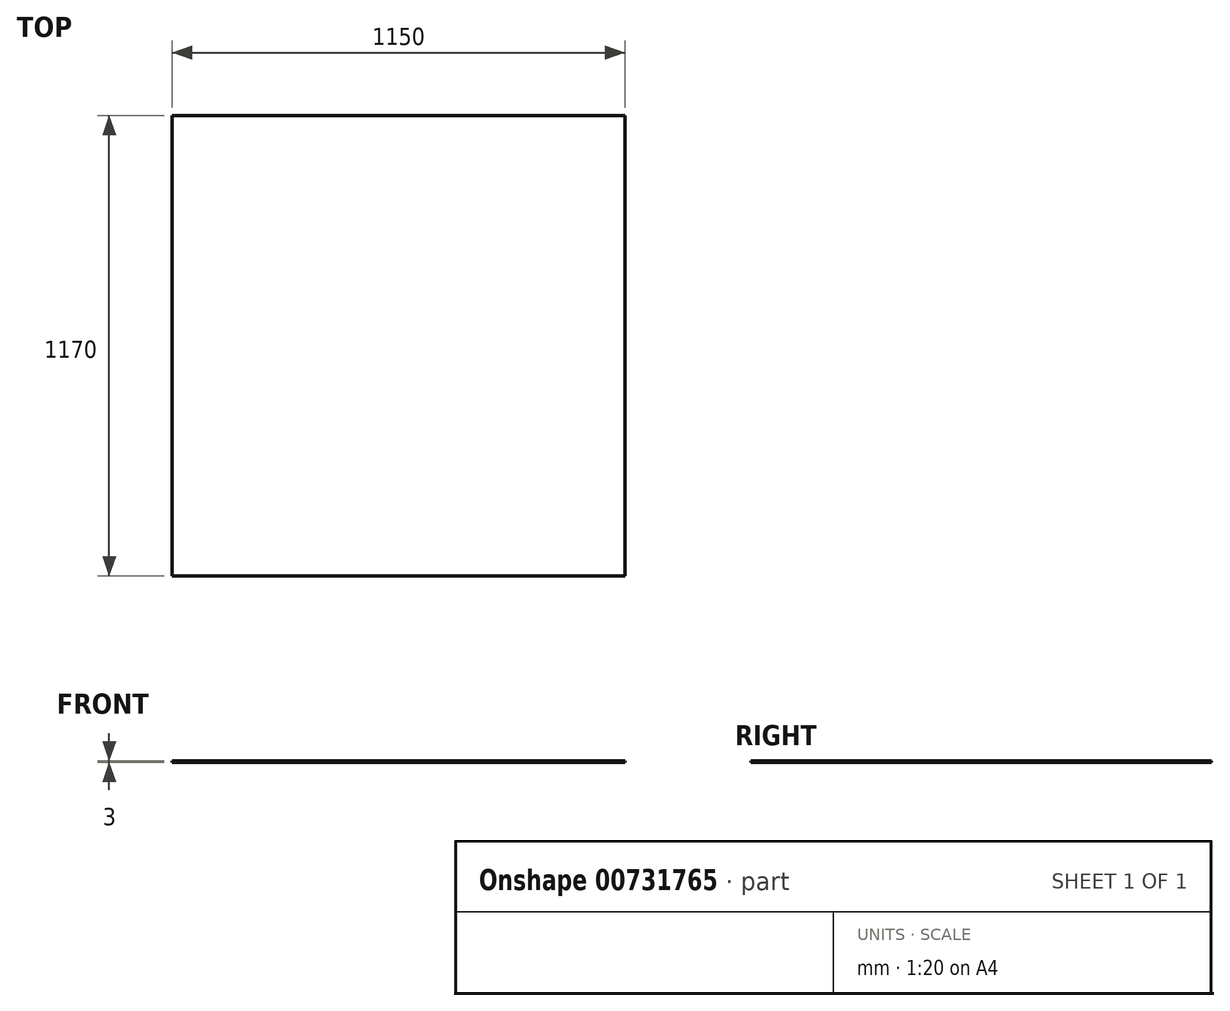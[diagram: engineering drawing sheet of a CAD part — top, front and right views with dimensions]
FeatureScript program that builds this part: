
annotation { "Feature Type Name" : "Feature", "Feature Type Description" : "" }
export const myFeature = defineFeature(function(context is Context, id is Id, definition is map)
    precondition{}
    {
        {
            var Q0;
            Q0=qCreatedBy(makeId("Top.planeOp"),FACE);
            var sketch = newSketch(context, id + "F0", { "sketchPlane" : qUnion([Q0])});
            skLineSegment(sketch, "E0.bottom", {"start": v(0, 0) * mm, "end": v(1150, 0) * mm});
            skLineSegment(sketch, "E0.top", {"start": v(0, 1170) * mm, "end": v(1150, 1170) * mm});
            skLineSegment(sketch, "E0.left", {"start": v(0, 0) * mm, "end": v(0, 1170) * mm});
            skLineSegment(sketch, "E0.right", {"start": v(1150, 0) * mm, "end": v(1150, 1170) * mm});
            skSolve(sketch);
        }
        {
            var Q0;
            Q0=makeQuery(id+"F0.imprint","IMPRINT",FACE,{"disambiguationData":[TD([[makeQuery(id+"F0.imprint","IMPRINT",EDGE,{"derivedFrom":sQuery(id+"F0.wireOp",EDGE,"E0.bottom")}),1.0]])]});
            extrude(context, id + "F1", {"entities" : qUnion([Q0]), "depth" : 3 * mm, "offsetDistance" : 25 * mm});
        }
    });
